# Revit family: 2069650(n) 300
name_source: partatom
category: Security Devices
units: mm (PartAtom-declared; Revit-internal decimal feet)

## family parameters
Always vertical = No
Cut with Voids When Loaded = No
Host = Wall
OmniClass Number = 23.85.30.14
OmniClass Title = Presence Detection/Registration
Room Calculation Point = No
Shared = Yes

## types (2) — shared parameters
zero-valued in all types: A, EF001992

## per-type parameters (varying)
- Type 1: CTN=0; EF000218=0 mm  [stored 0 ft]; EF000259=0; EF000551=0 mm  [stored 0 ft]; EF001322=0 mm  [stored 0 ft]; EF001323=0 mm  [stored 0 ft]; EF003843=0 mm  [stored 0 ft]; EF003882=0; EF006589=0; EF006590=0; EF008011=0 mm  [stored 0 ft]; EF010517=0 mm  [stored 0 ft]; EF010886=0 mm  [stored 0 ft]; EF011019=0 mm  [stored 0 ft]; EF011020=0 mm  [stored 0 ft]; EF012278=0 mm  [stored 0 ft]; LOG=0; NOCUPEROU=0; PRICEQUANTITY=0; QUANTITYINT=0; QUANTITYMIN=0
- 2069650: ARTICLENO=NB; BOMINFO=LINA; CATALOG=Theben; COO=CN; CTN=85365080; DEEPLINK_PRODUKTSEITE=http://www.theben.de; DESCLONG=KNX passive infrared motion detector for flush-mounted wall mounting, 1 channel light and 1 channel HVAC, KNX Data-Secure, with Theben cover frame, cover frame for integration into common switch ranges available as accessory, Rectangular detection area 170° up to 14x17 m, Automatic presence and brightness-dependent control for lighting, Switching or dimmable lighting in switching mode with and without daylight influence, 3 logic channels (AND, OR, XOR), Operation as fully or semi-automatic, switchable, Brightness switching value adjustable, Teach-in function, Switch-on delay and follow-up time adjustable, Limitation of the detection area possible, Integrated pushbutton freely parameterizable (blockable), Extension of the detection area by master/slave switching; DESCSHORT=KNX motion detector wall mounting flush-mounted, detection area 14 x 17 m, 1 x light, 1 x HVAC; EF000003=EV000383; EF000007=White; EF000010=Motion detector; EF000139=Untreated; EF000147=false; EF000218=24 mm  [stored 0.0787402 ft]; EF000259=2; EF000551=54 mm  [stored 0.177165 ft]; EF001098=true; EF001257=Thermoplast; EF001322=17000 mm  [stored 55.7743 ft]; EF001323=17000 mm  [stored 55.7743 ft]; EF001499=true; EF001500=false; EF001501=false; EF001504=true; EF002169=Plastic; EF003831=false; EF003843=17000 mm  [stored 55.7743 ft]; EF003876=true; EF003882=9010; EF003898=true; EF004530=false; EF006243=false; EF006311=false; EF006569=matt; EF006582=0, 170 °; EF006589=30; EF006590=60; EF007575=true; EF007667=false; EF008011=1100 mm; EF008855=false; EF009466=false; EF010517=20 mm  [stored 0.0656168 ft]; EF010886=10 mm  [stored 0.0328084 ft]; EF011019=45 mm  [stored 0.147638 ft]; EF011020=50 mm  [stored 0.164042 ft]; EF012278=40 mm  [stored 0.131234 ft]; EF016048=false; GEBRAUCHSANLEITUNG=http://www.theben.de; INTNO=4003468200407; LINA=2069650; LOG=300; MANUID=2069650; MANUNAME=Theben AG; MANUTYPEDESC=theMura S180 KNX UP WH; Manufacturer=Theben; Model=2069650; NB=2069650(N) 300; NBSYN=$MANUID.($SA.) $LOG.; NN=Presence detector KNX; NOCUPEROU=1; PRICEQUANTITY=1; PRODUKTDATENBLATT=http://www.theben.de; QUANTITYINT=1; QUANTITYMIN=1; REACH_ERKLAERUNG=http://www.theben.de; REMARKS=ERP-GROUP 252; SA=None; SUPPLIER=THEBEN; SUPPLIERALTNO=2069650

note: [stored X ft] marks values corroborated as IEEE doubles in the binary element streams (Revit-internal decimal feet)

## geometry (parser evidence)
native form markers: Sweep x6
no freeform markers — native parametric forms only
